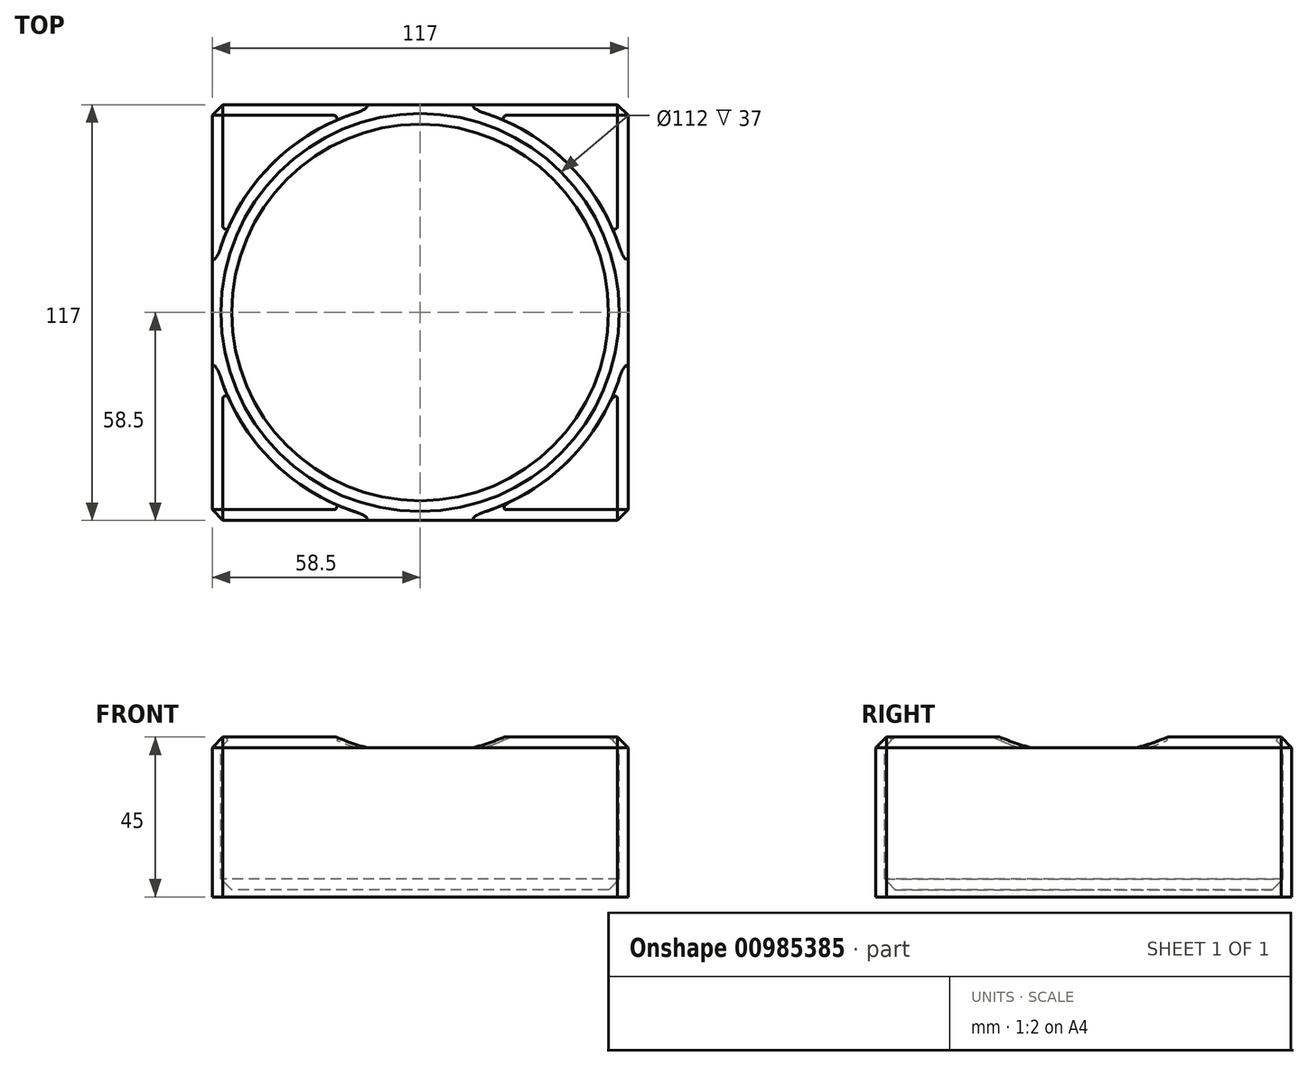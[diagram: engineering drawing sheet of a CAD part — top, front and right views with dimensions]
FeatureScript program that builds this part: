
annotation { "Feature Type Name" : "Feature", "Feature Type Description" : "" }
export const myFeature = defineFeature(function(context is Context, id is Id, definition is map)
    precondition{}
    {
        {
            var Q0;
            Q0=qCreatedBy(makeId("Top.planeOp"),FACE);
            var sketch = newSketch(context, id + "F0", { "sketchPlane" : qUnion([Q0])});
            skLineSegment(sketch, "E0.bottom", {"start": v(-58.5, 58.5) * mm, "end": v(58.5, 58.5) * mm});
            skLineSegment(sketch, "E0.top", {"start": v(-58.5, -58.5) * mm, "end": v(58.5, -58.5) * mm});
            skLineSegment(sketch, "E0.left", {"start": v(-58.5, 58.5) * mm, "end": v(-58.5, -58.5) * mm});
            skLineSegment(sketch, "E0.right", {"start": v(58.5, 58.5) * mm, "end": v(58.5, -58.5) * mm});
            skSolve(sketch);
        }
        {
            var Q0;
            Q0=makeQuery(id+"F0.imprint","IMPRINT",FACE,{"disambiguationData":[TD([[makeQuery(id+"F0.imprint","IMPRINT",EDGE,{"derivedFrom":sQuery(id+"F0.wireOp",EDGE,"E0.bottom")}),-1.0]])]});
            extrude(context, id + "F1", {"entities" : qUnion([Q0]), "depth" : 45 * mm, "offsetDistance" : 25 * mm});
        }
        {
            var Q0;
            {var subQ0=sQuery(id+"F0.wireOp",EDGE,"E0.bottom");var subQ1=sQuery(id+"F0.wireOp",EDGE,"E0.left");Q0=makeQuery(id+"F4.boolean.opBoolean","SPLIT",EDGE,{"disambiguationData":[TD([makeQuery(id+"F1.opExtrude","SWEPT_FACE",FACE,{"disambiguationData":[OSD([subQ0])]})])],"derivedFrom":makeQuery(id+"F1.opExtrude","CAP_EDGE",EDGE,{"disambiguationData":[OSD([subQ1])],"isStart":false})});}
            var Q1;
            Q1=makeQuery(id+"F1.opExtrude","CAP_EDGE",EDGE,{"disambiguationData":[OSD([sQuery(id+"F0.wireOp",EDGE,"E0.top")])],"isStart":false});
            var Q2;
            Q2=makeQuery(id+"F1.opExtrude","CAP_EDGE",EDGE,{"disambiguationData":[OSD([sQuery(id+"F0.wireOp",EDGE,"E0.right")])],"isStart":false});
            var Q3;
            Q3=makeQuery(id+"F1.opExtrude","CAP_EDGE",EDGE,{"disambiguationData":[OSD([sQuery(id+"F0.wireOp",EDGE,"E0.bottom")])],"isStart":false});
            var Q4;
            Q4=makeQuery(id+"F1.opExtrude","SWEPT_EDGE",EDGE,{"disambiguationData":[OSD([sQuery(id+"F0.wireOp",EDGE,"E0.bottom"),sQuery(id+"F0.wireOp",EDGE,"E0.left")])]});
            var Q5;
            Q5=makeQuery(id+"F1.opExtrude","SWEPT_EDGE",EDGE,{"disambiguationData":[OSD([sQuery(id+"F0.wireOp",EDGE,"E0.bottom"),sQuery(id+"F0.wireOp",EDGE,"E0.right")])]});
            var Q6;
            Q6=makeQuery(id+"F1.opExtrude","SWEPT_EDGE",EDGE,{"disambiguationData":[OSD([sQuery(id+"F0.wireOp",EDGE,"E0.top"),sQuery(id+"F0.wireOp",EDGE,"E0.right")])]});
            var Q7;
            Q7=makeQuery(id+"F1.opExtrude","SWEPT_EDGE",EDGE,{"disambiguationData":[OSD([sQuery(id+"F0.wireOp",EDGE,"E0.top"),sQuery(id+"F0.wireOp",EDGE,"E0.left")])]});
            chamfer(context, id + "F2", {"entities" : qUnion([Q0, Q1, Q2, Q3, Q4, Q5, Q6, Q7]), "width" : 3 * mm, "tangentPropagation" : true});
        }
        {
            var Q0;
            Q0=makeQuery(id+"F1.opExtrude","CAP_FACE",FACE,{"disambiguationData":[OSD([sQuery(id+"F0.wireOp",EDGE,"E0.bottom"),sQuery(id+"F0.wireOp",EDGE,"E0.top"),sQuery(id+"F0.wireOp",EDGE,"E0.left"),sQuery(id+"F0.wireOp",EDGE,"E0.right")])],"isStart":false});
            var sketch = newSketch(context, id + "F3", { "sketchPlane" : qUnion([Q0])});
            skCircle(sketch, "E1", {"center": v(0, 0) * mm, "radius": 59 * mm});
            skSolve(sketch);
        }
        {
            var Q0;
            Q0 = qSketchRegion(id + "F3", true);
            extrude(context, id + "F4", {"entities" : qUnion([Q0]), "operationType" : NewBodyOperationType.REMOVE, "oppositeDirection" : true, "depth" : 3 * mm, "offsetDistance" : 25 * mm});
        }
        {
            var Q0;
            Q0=makeQuery(id+"F4.boolean.opBoolean","COPY",FACE,{"derivedFrom":makeQuery(id+"F4.opExtrude","CAP_FACE",FACE,{"disambiguationData":[OSD([sQuery(id+"F3.wireOp",EDGE,"E1")])],"isStart":false})});
            var sketch = newSketch(context, id + "F5", { "sketchPlane" : qUnion([Q0])});
            skCircle(sketch, "E2", {"center": v(0, 0) * mm, "radius": 56 * mm});
            skSolve(sketch);
        }
        {
            var Q0;
            Q0 = qSketchRegion(id + "F5", true);
            extrude(context, id + "F6", {"entities" : qUnion([Q0]), "operationType" : NewBodyOperationType.REMOVE, "endBound" : BoundingType.UP_TO_NEXT, "oppositeDirection" : true, "depth" : 25 * mm, "hasOffset" : true, "offsetDistance" : 2 * mm});
        }
        {
            var Q0;
            Q0=makeQuery(id+"F6.boolean.opBoolean","COPY",EDGE,{"derivedFrom":makeQuery(id+"F6.opExtrude","CAP_EDGE",EDGE,{"disambiguationData":[OSD([sQuery(id+"F5.wireOp",EDGE,"E2")])],"isStart":false})});
            chamfer(context, id + "F7", {"entities" : qUnion([Q0]), "width" : 3 * mm, "tangentPropagation" : true});
        }
        {
            var Q0;
            Q0=makeQuery(id+"F4.boolean.opBoolean","INTERSECT",EDGE,{"disambiguationData":[OD(0.0)],"derivedFrom":[makeQuery(id+"F2.opChamfer","BLEND_FACE",FACE,{"disambiguationData":[OSD([sQuery(id+"F0.wireOp",EDGE,"E0.left")])]}),makeQuery(id+"F4.opExtrude","SWEPT_FACE",FACE,{"disambiguationData":[OSD([sQuery(id+"F3.wireOp",EDGE,"E1")])]})]});
            var Q1;
            Q1=makeQuery(id+"F4.boolean.opBoolean","INTERSECT",EDGE,{"disambiguationData":[OD(1.0)],"derivedFrom":[makeQuery(id+"F2.opChamfer","BLEND_FACE",FACE,{"disambiguationData":[OSD([sQuery(id+"F0.wireOp",EDGE,"E0.bottom")])]}),makeQuery(id+"F4.opExtrude","SWEPT_FACE",FACE,{"disambiguationData":[OSD([sQuery(id+"F3.wireOp",EDGE,"E1")])]})]});
            var Q2;
            Q2=makeQuery(id+"F4.boolean.opBoolean","INTERSECT",EDGE,{"disambiguationData":[OD(0.0)],"derivedFrom":[makeQuery(id+"F2.opChamfer","BLEND_FACE",FACE,{"disambiguationData":[OSD([sQuery(id+"F0.wireOp",EDGE,"E0.right")])]}),makeQuery(id+"F4.opExtrude","SWEPT_FACE",FACE,{"disambiguationData":[OSD([sQuery(id+"F3.wireOp",EDGE,"E1")])]})]});
            var Q3;
            Q3=makeQuery(id+"F4.boolean.opBoolean","INTERSECT",EDGE,{"disambiguationData":[OD(0.0)],"derivedFrom":[makeQuery(id+"F2.opChamfer","BLEND_FACE",FACE,{"disambiguationData":[OSD([sQuery(id+"F0.wireOp",EDGE,"E0.bottom")])]}),makeQuery(id+"F4.opExtrude","SWEPT_FACE",FACE,{"disambiguationData":[OSD([sQuery(id+"F3.wireOp",EDGE,"E1")])]})]});
            var Q4;
            Q4=makeQuery(id+"F4.boolean.opBoolean","INTERSECT",EDGE,{"disambiguationData":[OD(0.0)],"derivedFrom":[makeQuery(id+"F2.opChamfer","BLEND_FACE",FACE,{"disambiguationData":[OSD([sQuery(id+"F0.wireOp",EDGE,"E0.top")])]}),makeQuery(id+"F4.opExtrude","SWEPT_FACE",FACE,{"disambiguationData":[OSD([sQuery(id+"F3.wireOp",EDGE,"E1")])]})]});
            var Q5;
            Q5=makeQuery(id+"F4.boolean.opBoolean","INTERSECT",EDGE,{"disambiguationData":[OD(1.0)],"derivedFrom":[makeQuery(id+"F2.opChamfer","BLEND_FACE",FACE,{"disambiguationData":[OSD([sQuery(id+"F0.wireOp",EDGE,"E0.top")])]}),makeQuery(id+"F4.opExtrude","SWEPT_FACE",FACE,{"disambiguationData":[OSD([sQuery(id+"F3.wireOp",EDGE,"E1")])]})]});
            var Q6;
            Q6=makeQuery(id+"F4.boolean.opBoolean","INTERSECT",EDGE,{"disambiguationData":[OD(1.0)],"derivedFrom":[makeQuery(id+"F2.opChamfer","BLEND_FACE",FACE,{"disambiguationData":[OSD([sQuery(id+"F0.wireOp",EDGE,"E0.right")])]}),makeQuery(id+"F4.opExtrude","SWEPT_FACE",FACE,{"disambiguationData":[OSD([sQuery(id+"F3.wireOp",EDGE,"E1")])]})]});
            var Q7;
            Q7=makeQuery(id+"F4.boolean.opBoolean","INTERSECT",EDGE,{"disambiguationData":[OD(1.0)],"derivedFrom":[makeQuery(id+"F2.opChamfer","BLEND_FACE",FACE,{"disambiguationData":[OSD([sQuery(id+"F0.wireOp",EDGE,"E0.left")])]}),makeQuery(id+"F4.opExtrude","SWEPT_FACE",FACE,{"disambiguationData":[OSD([sQuery(id+"F3.wireOp",EDGE,"E1")])]})]});
            var Q8;
            {var subQ0=sQuery(id+"F0.wireOp",EDGE,"E0.right");var subQ1=sQuery(id+"F0.wireOp",EDGE,"E0.bottom");var subQ2=sQuery(id+"F3.wireOp",EDGE,"E1");Q8=makeQuery(id+"F4.boolean.opBoolean","COPY",EDGE,{"disambiguationData":[TD([makeQuery(id+"F1.opExtrude","CAP_FACE",FACE,{"disambiguationData":[OSD([subQ1,sQuery(id+"F0.wireOp",EDGE,"E0.top"),sQuery(id+"F0.wireOp",EDGE,"E0.left"),subQ0])],"isStart":false}),makeQuery(id+"F2.opChamfer","BLEND_FACE",FACE,{"disambiguationData":[OSD([subQ1])]}),makeQuery(id+"F2.opChamfer","BLEND_FACE",FACE,{"disambiguationData":[OSD([subQ0])]}),makeQuery(id+"F4.opExtrude","SWEPT_FACE",FACE,{"disambiguationData":[OSD([subQ2])]})])],"derivedFrom":makeQuery(id+"F4.opExtrude","CAP_EDGE",EDGE,{"disambiguationData":[OSD([subQ2])],"isStart":true})});}
            var Q9;
            {var subQ0=sQuery(id+"F0.wireOp",EDGE,"E0.right");var subQ1=sQuery(id+"F0.wireOp",EDGE,"E0.top");var subQ2=sQuery(id+"F3.wireOp",EDGE,"E1");Q9=makeQuery(id+"F4.boolean.opBoolean","COPY",EDGE,{"disambiguationData":[TD([makeQuery(id+"F1.opExtrude","CAP_FACE",FACE,{"disambiguationData":[OSD([sQuery(id+"F0.wireOp",EDGE,"E0.bottom"),subQ1,sQuery(id+"F0.wireOp",EDGE,"E0.left"),subQ0])],"isStart":false}),makeQuery(id+"F2.opChamfer","BLEND_FACE",FACE,{"disambiguationData":[OSD([subQ1])]}),makeQuery(id+"F2.opChamfer","BLEND_FACE",FACE,{"disambiguationData":[OSD([subQ0])]}),makeQuery(id+"F4.opExtrude","SWEPT_FACE",FACE,{"disambiguationData":[OSD([subQ2])]})])],"derivedFrom":makeQuery(id+"F4.opExtrude","CAP_EDGE",EDGE,{"disambiguationData":[OSD([subQ2])],"isStart":true})});}
            var Q10;
            {var subQ0=sQuery(id+"F0.wireOp",EDGE,"E0.left");var subQ1=sQuery(id+"F0.wireOp",EDGE,"E0.top");var subQ2=sQuery(id+"F3.wireOp",EDGE,"E1");Q10=makeQuery(id+"F4.boolean.opBoolean","COPY",EDGE,{"disambiguationData":[TD([makeQuery(id+"F1.opExtrude","CAP_FACE",FACE,{"disambiguationData":[OSD([sQuery(id+"F0.wireOp",EDGE,"E0.bottom"),subQ1,subQ0,sQuery(id+"F0.wireOp",EDGE,"E0.right")])],"isStart":false}),makeQuery(id+"F2.opChamfer","BLEND_FACE",FACE,{"disambiguationData":[OSD([subQ1])]}),makeQuery(id+"F2.opChamfer","BLEND_FACE",FACE,{"disambiguationData":[OSD([subQ0])]}),makeQuery(id+"F4.opExtrude","SWEPT_FACE",FACE,{"disambiguationData":[OSD([subQ2])]})])],"derivedFrom":makeQuery(id+"F4.opExtrude","CAP_EDGE",EDGE,{"disambiguationData":[OSD([subQ2])],"isStart":true})});}
            var Q11;
            {var subQ0=sQuery(id+"F0.wireOp",EDGE,"E0.left");var subQ1=sQuery(id+"F0.wireOp",EDGE,"E0.bottom");var subQ2=sQuery(id+"F3.wireOp",EDGE,"E1");Q11=makeQuery(id+"F4.boolean.opBoolean","COPY",EDGE,{"disambiguationData":[TD([makeQuery(id+"F1.opExtrude","CAP_FACE",FACE,{"disambiguationData":[OSD([subQ1,sQuery(id+"F0.wireOp",EDGE,"E0.top"),subQ0,sQuery(id+"F0.wireOp",EDGE,"E0.right")])],"isStart":false}),makeQuery(id+"F2.opChamfer","BLEND_FACE",FACE,{"disambiguationData":[OSD([subQ1])]}),makeQuery(id+"F2.opChamfer","BLEND_FACE",FACE,{"disambiguationData":[OSD([subQ0])]}),makeQuery(id+"F4.opExtrude","SWEPT_FACE",FACE,{"disambiguationData":[OSD([subQ2])]})])],"derivedFrom":makeQuery(id+"F4.opExtrude","CAP_EDGE",EDGE,{"disambiguationData":[OSD([subQ2])],"isStart":true})});}
            var Q12;
            Q12=makeQuery(id+"F6.boolean.opBoolean","COPY",EDGE,{"derivedFrom":makeQuery(id+"F6.opExtrude","CAP_EDGE",EDGE,{"disambiguationData":[OSD([sQuery(id+"F5.wireOp",EDGE,"E2")])],"isStart":true})});
            fillet(context, id + "F8", {"entities" : qUnion([Q0, Q1, Q2, Q3, Q4, Q5, Q6, Q7, Q8, Q9, Q10, Q11, Q12]), "radius" : 1 * mm, "tangentPropagation" : true, "allowEdgeOverflow" : false});
        }
    });
